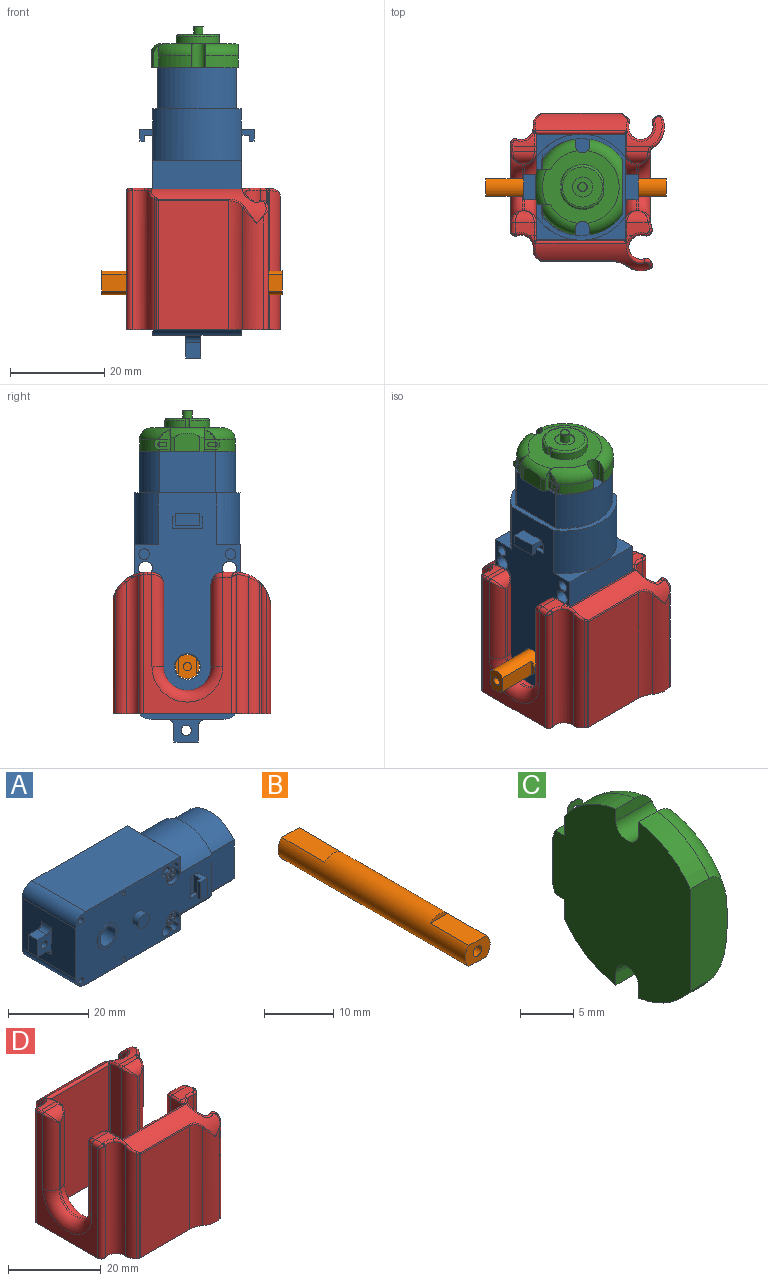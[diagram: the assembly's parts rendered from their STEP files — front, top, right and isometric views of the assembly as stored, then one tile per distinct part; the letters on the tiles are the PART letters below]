
ASSEMBLY  parts=4 mates=3
PART A: 126 faces, bbox 61.5x24.2x22.5 mm
  f0: torus R=1.4mm, axis (0,-1,0), area 4.7mm2, adj f2,f68
  f1: torus R=1.4mm, axis (0,-1,0), area 4.7mm2, adj f3,f66
  f2: cylinder r=1.7mm len=3.4mm, axis (0,1,0), area 12.8mm2, adj f0,f23,f67
  f3: cylinder r=1.7mm len=3.4mm, axis (0,1,0), area 12.8mm2, adj f1,f24,f65
  f4: cylinder r=2.25mm len=4.5mm, axis (0,-1,0), area 19.8mm2, adj f8,f9,f23,f26
  f5: cylinder r=2.25mm len=4.5mm, axis (0,-1,0), area 19.8mm2, adj f12,f13,f24,f26
  f6: cylinder r=1.12mm len=7.5mm, axis (0,1,0), area 53mm2, adj f37,f62
  f7: cylinder r=1.12mm len=7.5mm, axis (0,1,0), area 53mm2, adj f37,f61
  f8: cylinder r=1.5mm len=18.8mm, axis (0,-1,0), area 173.3mm2, adj f4,f23,f26,f37,f64
  f9: cylinder r=1.12mm len=7.5mm, axis (0,-1,0), area 48.7mm2, adj f4,f23,f26,f55,f64,f67
  f10: cylinder r=0.62mm len=7.5mm, axis (0,-1,0), area 29.5mm2, adj f26,f54
  f11: cylinder r=0.9mm len=7.5mm, axis (0,-1,0), area 42.4mm2, adj f26,f53
  f12: cylinder r=1.12mm len=7.5mm, axis (0,-1,0), area 48.7mm2, adj f5,f24,f26,f52,f63,f65
  f13: cylinder r=1.5mm len=18.8mm, axis (0,-1,0), area 173.3mm2, adj f5,f24,f26,f37,f63
  f14: cylinder r=0.62mm len=7.5mm, axis (0,-1,0), area 29.5mm2, adj f26,f51
  f15: cylinder r=0.9mm len=7.5mm, axis (0,-1,0), area 42.4mm2, adj f26,f50
  f16: cylinder r=2mm len=4mm, axis (0,1,0), area 25.1mm2, adj f26,f49
  f17: cylinder r=3.62mm len=7.25mm, axis (0,1,0), area 5.7mm2, adj f26,f48
  f18: cylinder r=2.75mm len=19.05mm, axis (0,1,0), area 329.2mm2, adj f37,f48
  f19: cylinder r=1.1mm len=3.2mm, axis (0,1,0), area 22.1mm2, adj f38,f40
  f20: plane 5.25x2.7mm, normal (-1,0,0), area 14.2mm2, adj f107,f113,f115,f125
  f21: plane 1x0.63mm, normal (-1,0,0), area 0.6mm2, adj f37,f109,f112,f118
  f22: plane 1x0.63mm, normal (-1,0,0), area 0.6mm2, adj f26,f103,f107,f113
  f23: plane 4.5x4.48mm, normal (0,-1,0), area 5.4mm2, adj f2,f4,f8,f9,f64
  f24: plane 4.5x4.48mm, normal (0,-1,0), area 5.4mm2, adj f3,f5,f12,f13,f63
  f25: plane 22.5x18.8mm, normal (1,0,0), area 66.1mm2, adj f26,f27,f37,f47,f56,f57,f58,f59
  f26: plane 48x22.3mm, normal (0,-1,0), area 823.8mm2, adj f4,f5,f8,f9,f10,f11,f12,f13
  f27: cylinder r=11.25mm len=18.8mm, axis (-1,0,0), area 244.8mm2, adj f25,f26,f28,f29,f37,f45
  f28: plane 7.9x4.97mm, normal (1,0,0), area 13.3mm2, adj f27,f33,f37
  f29: plane 7.9x4.97mm, normal (1,0,0), area 13.3mm2, adj f26,f27,f33
  f30: plane 7.9x4.97mm, normal (1,0,0), area 13.3mm2, adj f26,f36,f47
  f31: plane 7.9x4.97mm, normal (1,0,0), area 13.3mm2, adj f36,f37,f47
  f32: plane 18.8x15.3mm, normal (-1,0,0), area 261.4mm2, adj f26,f34,f35,f37,f38,f40,f43,f44
  f33: plane 33.5x18.8mm, normal (0,0,1), area 629.8mm2, adj f26,f28,f29,f34,f37,f45
  f34: cylinder r=3.5mm len=18.8mm, axis (0,1,0), area 103.4mm2, adj f26,f32,f33,f37
  f35: cylinder r=3.5mm len=18.8mm, axis (0,1,0), area 103.4mm2, adj f26,f32,f36,f37
  f36: plane 33.5x18.8mm, normal (0,0,-1), area 629.8mm2, adj f26,f30,f31,f35,f37,f46
  f37: plane 48x22.3mm, normal (0,1,0), area 890.3mm2, adj f6,f7,f8,f13,f18,f21,f25,f27
  f38: plane 8.2x4.8mm, normal (0,-1,0), area 22.1mm2, adj f19,f32,f39,f41,f42,f43,f44
  f39: plane 3.3x3.2mm, normal (0,0,1), area 10.6mm2, adj f38,f40,f42,f44
  f40: plane 8.2x4.8mm, normal (0,1,0), area 22.1mm2, adj f19,f32,f39,f41,f42,f43,f44
  f41: plane 3.3x3.2mm, normal (0,0,-1), area 10.6mm2, adj f38,f40,f42,f43
  f42: plane 5.2x3.2mm, normal (-1,0,0), area 16.6mm2, adj f38,f39,f40,f41
  f43: cylinder r=1.5mm len=3.2mm, axis (0,1,0), area 7.5mm2, adj f32,f38,f40,f41
  f44: cylinder r=1.5mm len=3.2mm, axis (0,-1,0), area 7.5mm2, adj f32,f38,f39,f40
  f45: plane 2.99x0.1mm, normal (-1,0,0), area 0.2mm2, adj f27,f33
  f46: plane 2.99x0.1mm, normal (-1,0,0), area 0.2mm2, adj f36,f47
  f47: cylinder r=11.25mm len=18.8mm, axis (-1,0,0), area 244.8mm2, adj f25,f26,f30,f31,f37,f46
  f48: plane 7.25x7.25mm, normal (0,-1,0), area 17.5mm2, adj f17,f18
  f49: plane 4x4mm, normal (0,-1,0), area 12.6mm2, adj f16
  f50: plane 1.8x1.8mm, normal (0,-1,0), area 2.5mm2, adj f15
  f51: plane 1.25x1.25mm, normal (0,-1,0), area 1.2mm2, adj f14
  f52: plane 2.25x2.25mm, normal (0,-1,0), area 4mm2, adj f12
  f53: plane 1.8x1.8mm, normal (0,-1,0), area 2.5mm2, adj f11
  f54: plane 1.25x1.25mm, normal (0,-1,0), area 1.2mm2, adj f10
  f55: plane 2.25x2.25mm, normal (0,-1,0), area 4mm2, adj f9
  f56: cylinder r=10.25mm len=16.8mm, axis (-1,0,0), area 172.1mm2, adj f25,f57,f59,f60
  f57: plane 11.75x8.74mm, normal (0,1,0), area 102.7mm2, adj f25,f56,f58,f60
  f58: cylinder r=10.25mm len=16.8mm, axis (-1,0,0), area 172.1mm2, adj f25,f57,f59,f60
  f59: plane 11.75x8.74mm, normal (0,-1,0), area 102.7mm2, adj f25,f56,f58,f60
  f60: plane 20.5x16.8mm, normal (1,0,0), area 300.5mm2, adj f56,f57,f58,f59
  f61: plane 2.25x2.25mm, normal (0,1,0), area 4mm2, adj f7
  f62: plane 2.25x2.25mm, normal (0,1,0), area 4mm2, adj f6
  f63: cylinder r=2.25mm len=2mm, axis (0,-1,0), area 0.9mm2, adj f12,f13,f24,f26
  f64: cylinder r=2.25mm len=2mm, axis (0,-1,0), area 0.9mm2, adj f8,f9,f23,f26
  f65: plane 0.76x0.22mm, normal (0,1,0), area 0.1mm2, adj f3,f12
  f66: plane 2.8x2.8mm, normal (0,-1,0), area 3.6mm2, adj f1,f69,f70,f71,f72,f73,f74,f75
  f67: plane 0.76x0.22mm, normal (0,1,0), area 0.1mm2, adj f2,f9
  f68: plane 2.8x2.8mm, normal (0,-1,0), area 3.6mm2, adj f0,f82,f83,f84,f85,f86,f87,f88
  f69: plane 1.5x0.84mm, normal (0.99,-0.16,0), area 0.9mm2, adj f66,f70,f81,f100
  f70: plane 1.5x0.6mm, normal (0,-0.16,-0.99), area 0.6mm2, adj f66,f69,f71,f81
  f71: plane 1.5x0.84mm, normal (-0.99,-0.16,0), area 0.9mm2, adj f66,f70,f81,f99
  f72: plane 1.5x0.84mm, normal (0,-0.16,-0.99), area 0.9mm2, adj f66,f73,f81,f99
  f73: plane 1.5x0.6mm, normal (-0.99,-0.16,0), area 0.6mm2, adj f66,f72,f74,f81
  f74: plane 1.5x0.84mm, normal (0,-0.16,0.99), area 0.9mm2, adj f66,f73,f81,f102
  f75: plane 1.5x0.84mm, normal (-0.99,-0.16,0), area 0.9mm2, adj f66,f76,f81,f102
  f76: plane 1.5x0.6mm, normal (0,-0.16,0.99), area 0.6mm2, adj f66,f75,f77,f81
  f77: plane 1.5x0.84mm, normal (0.99,-0.16,0), area 0.9mm2, adj f66,f76,f81,f101
  f78: plane 1.5x0.84mm, normal (0,-0.16,0.99), area 0.9mm2, adj f66,f79,f81,f101
  f79: plane 1.5x0.6mm, normal (0.99,-0.16,0), area 0.6mm2, adj f66,f78,f80,f81
  f80: plane 1.5x0.84mm, normal (0,-0.16,-0.99), area 0.9mm2, adj f66,f79,f81,f100
  f81: plane 1.93x1.93mm, normal (0,-1,0), area 0.5mm2, adj f69,f70,f71,f72,f73,f74,f75,f76
  f82: plane 1.5x0.84mm, normal (0,-0.16,0.99), area 0.9mm2, adj f68,f83,f94,f98
  f83: plane 1.5x0.6mm, normal (0.99,-0.16,0), area 0.6mm2, adj f68,f82,f84,f94
  f84: plane 1.5x0.84mm, normal (0,-0.16,-0.99), area 0.9mm2, adj f68,f83,f94,f96
  f85: plane 1.5x0.84mm, normal (0.99,-0.16,0), area 0.9mm2, adj f68,f86,f94,f96
  f86: plane 1.5x0.6mm, normal (0,-0.16,-0.99), area 0.6mm2, adj f68,f85,f87,f94
  f87: plane 1.5x0.84mm, normal (-0.99,-0.16,0), area 0.9mm2, adj f68,f86,f94,f95
  f88: plane 1.5x0.84mm, normal (0,-0.16,-0.99), area 0.9mm2, adj f68,f89,f94,f95
  f89: plane 1.5x0.6mm, normal (-0.99,-0.16,0), area 0.6mm2, adj f68,f88,f90,f94
  f90: plane 1.5x0.84mm, normal (0,-0.16,0.99), area 0.9mm2, adj f68,f89,f94,f97
  f91: plane 1.5x0.84mm, normal (-0.99,-0.16,0), area 0.9mm2, adj f68,f92,f94,f97
  f92: plane 1.5x0.6mm, normal (0,-0.16,0.99), area 0.6mm2, adj f68,f91,f93,f94
  f93: plane 1.5x0.84mm, normal (0.99,-0.16,0), area 0.9mm2, adj f68,f92,f94,f98
  f94: plane 1.93x1.93mm, normal (0,-1,0), area 0.5mm2, adj f82,f83,f84,f85,f86,f87,f88,f89
  f95: cylinder r=0.3mm len=1.54mm, axis (0.15,-0.98,0.15), area 0.7mm2, adj f68,f87,f88,f94
  f96: cylinder r=0.3mm len=1.54mm, axis (-0.15,-0.98,0.15), area 0.7mm2, adj f68,f84,f85,f94
  f97: cylinder r=0.3mm len=1.54mm, axis (0.15,-0.98,-0.15), area 0.7mm2, adj f68,f90,f91,f94
  f98: cylinder r=0.3mm len=1.54mm, axis (-0.15,-0.98,-0.15), area 0.7mm2, adj f68,f82,f93,f94
  f99: cylinder r=0.3mm len=1.54mm, axis (0.15,-0.98,0.15), area 0.7mm2, adj f66,f71,f72,f81
  f100: cylinder r=0.3mm len=1.54mm, axis (-0.15,-0.98,0.15), area 0.7mm2, adj f66,f69,f80,f81
  f101: cylinder r=0.3mm len=1.54mm, axis (-0.15,-0.98,-0.15), area 0.7mm2, adj f66,f77,f78,f81
  f102: cylinder r=0.3mm len=1.54mm, axis (0.15,-0.98,-0.15), area 0.7mm2, adj f66,f74,f75,f81
  f103: plane 2.5x1mm, normal (0,0,-1), area 2.5mm2, adj f22,f26,f106,f107
  f104: plane 1x0.63mm, normal (-1,0,0), area 0.6mm2, adj f26,f105,f107,f115
  f105: plane 2.5x1mm, normal (0,0,1), area 2.5mm2, adj f26,f104,f106,f107
  f106: plane 6.5x1mm, normal (1,0,0), area 6.5mm2, adj f26,f103,f105,f107
  f107: plane 6.5x2.5mm, normal (0,-1,0), area 12.8mm2, adj f20,f22,f103,f104,f105,f106,f113,f115
  f108: plane 1x0.63mm, normal (-1,0,0), area 0.6mm2, adj f37,f111,f112,f119
  f109: plane 2.5x1mm, normal (0,0,-1), area 2.5mm2, adj f21,f37,f110,f112
  f110: plane 6.5x1mm, normal (1,0,0), area 6.5mm2, adj f37,f109,f111,f112
  f111: plane 2.5x1mm, normal (0,0,1), area 2.5mm2, adj f37,f108,f110,f112
  f112: plane 6.5x2.5mm, normal (0,1,0), area 12.8mm2, adj f21,f108,f109,f110,f111,f118,f119,f120
  f113: plane 3.7x2.5mm, normal (0,0,1), area 5.4mm2, adj f20,f22,f26,f107,f114,f116,f124,f125
  f114: plane 5.25x2.7mm, normal (1,0,0), area 14.2mm2, adj f26,f113,f115,f116
  f115: plane 3.7x2.5mm, normal (0,0,-1), area 5.4mm2, adj f20,f26,f104,f107,f114,f116,f124,f125
  f116: plane 5.25x2.5mm, normal (0,-1,0), area 13.1mm2, adj f113,f114,f115,f124
  f117: plane 5.25x2.7mm, normal (1,0,0), area 14.2mm2, adj f37,f118,f119,f121
  f118: plane 3.7x2.5mm, normal (0,0,1), area 5.4mm2, adj f21,f37,f112,f117,f120,f121,f122,f123
  f119: plane 3.7x2.5mm, normal (0,0,-1), area 5.4mm2, adj f37,f108,f112,f117,f120,f121,f122,f123
  f120: plane 5.25x2.7mm, normal (-1,0,0), area 14.2mm2, adj f112,f118,f119,f123
  f121: plane 5.25x2.5mm, normal (0,1,0), area 13.1mm2, adj f117,f118,f119,f122
  f122: plane 5.25x1mm, normal (-1,0,0), area 5.3mm2, adj f118,f119,f121,f123
  f123: plane 5.25x1.2mm, normal (0,-1,0), area 6.3mm2, adj f118,f119,f120,f122
  f124: plane 5.25x1mm, normal (-1,0,0), area 5.2mm2, adj f113,f115,f116,f125
  f125: plane 5.25x1.2mm, normal (0,1,0), area 6.3mm2, adj f20,f113,f115,f124
PART B: 15 faces, bbox 5.1x38.2x5.1 mm
  f0: cylinder r=0.88mm len=8.75mm, axis (0,1,0), area 48.1mm2, adj f4,f14
  f1: cylinder r=0.88mm len=7.85mm, axis (0,-1,0), area 43.2mm2, adj f3,f5
  f2: cylinder r=2.55mm len=38.2mm, axis (0,1,0), area 483.5mm2, adj f3,f4,f6,f7,f8,f9,f10,f11
  f3: plane 5.1x3.7mm, normal (0,-1,0), area 14.6mm2, adj f1,f2,f6,f8
  f4: plane 5.1x3.7mm, normal (0,1,0), area 14.6mm2, adj f0,f2,f10,f12
  f5: plane 1.75x1.75mm, normal (0,-1,0), area 2.4mm2, adj f1
  f6: plane 7.85x3.51mm, normal (0,0,1), area 27.6mm2, adj f2,f3,f7
  f7: plane 3.51x0.7mm, normal (0,-1,0), area 1.7mm2, adj f2,f6
  f8: plane 7.85x3.51mm, normal (0,0,-1), area 27.6mm2, adj f2,f3,f9
  f9: plane 3.51x0.7mm, normal (0,-1,0), area 1.7mm2, adj f2,f8
  f10: plane 8.75x3.51mm, normal (0,0,1), area 30.7mm2, adj f2,f4,f11
  f11: plane 3.51x0.7mm, normal (0,1,0), area 1.7mm2, adj f2,f10
  f12: plane 8.75x3.51mm, normal (0,0,-1), area 30.7mm2, adj f2,f4,f13
  f13: plane 3.51x0.7mm, normal (0,1,0), area 1.7mm2, adj f2,f12
  f14: plane 1.75x1.75mm, normal (0,1,0), area 2.4mm2, adj f0
PART C: 61 faces, bbox 9.7x22.2x22.9 mm
  f0: cylinder r=0.43mm len=0.86mm, axis (0,-1,0), area 0.1mm2, adj f51,f52,f58,f60
  f1: cylinder r=0.43mm len=0.86mm, axis (0,-1,0), area 0.1mm2, adj f22,f40,f47,f48
  f2: torus R=0.9mm, axis (1,0,0), area 1mm2, adj f3,f37
  f3: cylinder r=1mm len=2mm, axis (-1,0,0), area 11.9mm2, adj f2,f16
  f4: cylinder r=2.12mm len=4.25mm, axis (1,0,0), area 2.7mm2, adj f16,f36
  f5: torus R=4.25mm, axis (1,0,0), area 20.7mm2, adj f6,f33,f34,f35,f36
  f6: cylinder r=0.5mm len=2mm, axis (-1,0,0), area 2.7mm2, adj f5,f13,f33,f34
  f7: plane 3.09x2.95mm, normal (0,1,0), area 3.3mm2, adj f9,f32,f53
  f8: plane 2.2x0.5mm, normal (0,1,0), area 1.1mm2, adj f9,f21,f29,f57
  f9: plane 5.29x3.04mm, normal (0,0,-1), area 4.7mm2, adj f7,f8,f13,f29,f32,f38,f50,f52
  f10: plane 1.54x0.86mm, normal (0,1,0), area 1.2mm2, adj f21,f58,f59,f60
  f11: plane 2.2x0.5mm, normal (0,1,0), area 1.1mm2, adj f15,f23,f29,f41
  f12: plane 3.09x2.95mm, normal (0,1,0), area 3.3mm2, adj f15,f30,f45
  f13: plane 16.23x15.36mm, normal (1,0,0), area 123.2mm2, adj f6,f9,f15,f19,f25,f30,f31,f32
  f14: plane 5.31x3.87mm, normal (0,1,0), area 19.3mm2, adj f29,f38,f49,f50
  f15: plane 5.29x3.04mm, normal (0,0,1), area 4.7mm2, adj f11,f12,f13,f29,f30,f38,f40,f41
  f16: plane 4.25x4.25mm, normal (1,0,0), area 11mm2, adj f3,f4
  f17: cylinder r=10.25mm len=6.9mm, axis (-1,0,0), area 20.9mm2, adj f18,f28,f29,f31
  f18: plane 4.85x1.51mm, normal (0,1,0), area 5.7mm2, adj f17,f19,f29,f31
  f19: cylinder r=1.5mm len=5mm, axis (-1,0,0), area 23.2mm2, adj f13,f18,f20,f29,f31,f32
  f20: plane 4.85x1.51mm, normal (0,-1,0), area 5.7mm2, adj f19,f21,f29,f32
  f21: cylinder r=10.25mm len=6.9mm, axis (-1,0,0), area 20.9mm2, adj f8,f10,f20,f29,f32,f51
  f22: plane 1.54x0.86mm, normal (0,1,0), area 1.2mm2, adj f1,f23,f47,f48
  f23: cylinder r=10.25mm len=6.9mm, axis (-1,0,0), area 20.9mm2, adj f11,f22,f24,f29,f30,f39
  f24: plane 4.85x1.51mm, normal (0,-1,0), area 5.7mm2, adj f23,f25,f29,f30
  f25: cylinder r=1.5mm len=5mm, axis (-1,0,0), area 23.2mm2, adj f13,f24,f26,f29,f30,f31
  f26: plane 4.85x1.51mm, normal (0,1,0), area 5.7mm2, adj f25,f27,f29,f31
  f27: cylinder r=10.25mm len=6.9mm, axis (-1,0,0), area 20.9mm2, adj f26,f28,f29,f31
  f28: plane 11.75x4.92mm, normal (0,-1,0), area 52.9mm2, adj f17,f27,f29,f31
  f29: plane 20.28x18.3mm, normal (-1,0,0), area 295.4mm2, adj f8,f9,f11,f14,f15,f17,f18,f19
  f30: torus R=7.75mm, axis (1,0,0), area 33.7mm2, adj f12,f13,f15,f23,f24,f25
  f31: torus R=7.75mm, axis (1,0,0), area 72.9mm2, adj f13,f17,f18,f19,f25,f26,f27,f28
  f32: torus R=7.75mm, axis (1,0,0), area 33.7mm2, adj f7,f9,f13,f19,f20,f21
  f33: cylinder r=4.75mm len=9.12mm, axis (-1,0,0), area 18.9mm2, adj f5,f6,f13,f35
  f34: cylinder r=4.75mm len=9.12mm, axis (-1,0,0), area 18.9mm2, adj f5,f6,f13,f35
  f35: plane 4.08x2.48mm, normal (0,-1,0), area 6.8mm2, adj f5,f13,f33,f34
  f36: plane 8.5x8.5mm, normal (1,0,0), area 42.6mm2, adj f4,f5
  f37: plane 1.8x1.8mm, normal (1,0,0), area 2.5mm2, adj f2
  f38: revolved ~8.87x2.61mm, area 18mm2, adj f9,f13,f14,f15,f49,f50
  f39: plane 2x1.03mm, normal (0,-1,0), area 1.5mm2, adj f23,f41,f42,f43,f44,f45,f46,f47
  f40: plane 3.23x2mm, normal (0,1,0), area 4.7mm2, adj f1,f15,f41,f42,f43,f44,f45,f46
  f41: plane 2.73x0.1mm, normal (-1,0,0), area 0.3mm2, adj f11,f15,f39,f40,f42
  f42: plane 0.5x0.5mm, normal (-0.71,0,0.71), area 0.1mm2, adj f39,f40,f41,f43
  f43: plane 1x0.1mm, normal (0,0,1), area 0.1mm2, adj f39,f40,f42,f44
  f44: plane 0.5x0.5mm, normal (0.71,0,0.71), area 0.1mm2, adj f39,f40,f43,f45
  f45: plane 2.73x0.1mm, normal (1,0,0), area 0.3mm2, adj f12,f15,f39,f40,f44
  f46: cylinder r=0.43mm len=0.86mm, axis (0,-1,0), area 0.1mm2, adj f39,f40,f47,f48
  f47: plane 1.14x0.1mm, normal (-1,0,0), area 0.1mm2, adj f1,f22,f39,f40,f46
  f48: plane 1.14x0.1mm, normal (1,0,0), area 0.1mm2, adj f1,f22,f39,f40,f46
  f49: cylinder r=10.25mm len=3mm, axis (1,0,0), area 3.2mm2, adj f14,f15,f29,f38
  f50: cylinder r=10.25mm len=3mm, axis (1,0,0), area 3.2mm2, adj f9,f14,f29,f38
  f51: plane 2x1.03mm, normal (0,-1,0), area 1.5mm2, adj f0,f21,f53,f54,f55,f56,f57,f58
  f52: plane 3.23x2mm, normal (0,1,0), area 4.7mm2, adj f0,f9,f53,f54,f55,f56,f57,f58
  f53: plane 2.73x0.1mm, normal (1,0,0), area 0.3mm2, adj f7,f9,f51,f52,f54
  f54: plane 0.5x0.5mm, normal (0.71,0,-0.71), area 0.1mm2, adj f51,f52,f53,f55
  f55: plane 1x0.1mm, normal (0,0,-1), area 0.1mm2, adj f51,f52,f54,f56
  f56: plane 0.5x0.5mm, normal (-0.71,0,-0.71), area 0.1mm2, adj f51,f52,f55,f57
  f57: plane 2.73x0.1mm, normal (-1,0,0), area 0.3mm2, adj f8,f9,f51,f52,f56
  f58: plane 1.14x0.1mm, normal (1,0,0), area 0.1mm2, adj f0,f10,f51,f52,f59
  f59: cylinder r=0.43mm len=0.86mm, axis (0,-1,0), area 0.1mm2, adj f10,f52,f58,f60
  f60: plane 1.14x0.1mm, normal (-1,0,0), area 0.1mm2, adj f0,f10,f51,f52,f59
PART D: 176 faces, bbox 32.6x33.5x33 mm
  f0: plane 33.4x32.6mm, normal (0,0,-1), area 424.7mm2, adj f3,f4,f7,f8,f9,f10,f11,f13
  f1: cylinder r=7.5mm len=4.5mm, axis (-1,0,0), area 7.1mm2, adj f6,f92,f137,f138,f139
  f2: cylinder r=7.5mm len=1.32mm, axis (-1,0,0), area 0.7mm2, adj f25,f85,f87
  f3: plane 29.5x22.12mm, normal (1,0,0), area 269.2mm2, adj f0,f34,f35,f37,f82,f85,f91,f92
  f4: plane 29.5x22.12mm, normal (-1,0,0), area 269.2mm2, adj f0,f46,f48,f49,f81,f83,f95,f96
  f5: plane 4.91x1.03mm, normal (0,0,1), area 4.8mm2, adj f32,f44,f70,f95
  f6: plane 4.5x1.03mm, normal (0,0,1), area 4.6mm2, adj f1,f36,f91,f140
  f7: cylinder r=2.58mm len=29.41mm, axis (0,0,-1), area 150.8mm2, adj f0,f51,f114,f133,f135,f137
  f8: cylinder r=2.58mm len=29.5mm, axis (0,0,-1), area 152.3mm2, adj f0,f52,f84,f87,f110
  f9: plane 27.73x0.56mm, normal (-0.58,-0.82,0), area 18.9mm2, adj f0,f52,f89,f146
  f10: plane 27.35x15.02mm, normal (0,-1,0), area 410.7mm2, adj f0,f67,f144,f146
  f11: cylinder r=5mm len=25.89mm, axis (0,0,-1), area 111.4mm2, adj f0,f56,f67,f115,f142
  f12: plane 26.55x0.02mm, normal (0.82,0.58,0), area 0.7mm2, adj f54,f56,f117
  f13: cylinder r=2.58mm len=29.5mm, axis (0,0,-1), area 274mm2, adj f0,f54,f55,f119,f120
  f14: plane 29.5x0.1mm, normal (0.82,-0.58,0), area 3.8mm2, adj f0,f55,f60,f122
  f15: cylinder r=5mm len=29.49mm, axis (0,0,-1), area 190.4mm2, adj f0,f57,f61,f62,f63,f72
  f16: plane 26.33x0.02mm, normal (-0.58,0.82,0), area 0.7mm2, adj f57,f58,f74
  f17: cylinder r=2.58mm len=27.31mm, axis (0,0,-1), area 262.4mm2, adj f0,f58,f59,f76
  f18: plane 26.33x1.09mm, normal (0.58,0.82,0), area 34.1mm2, adj f0,f59,f78,f127
  f19: plane 29.33x18.2mm, normal (0,1,0), area 533.7mm2, adj f0,f86,f100,f103
  f20: plane 28.73x18.2mm, normal (0,-1,0), area 522.9mm2, adj f0,f94,f97,f106
  f21: plane 24.55x15.6mm, normal (0,1,0), area 383mm2, adj f0,f50,f53,f130
  f22: plane 4.92x2.68mm, normal (0,0,1), area 11.1mm2, adj f33,f47,f81,f120,f121,f122,f123,f124
  f23: plane 29.5x18.67mm, normal (-1,0,0), area 168.8mm2, adj f0,f38,f40,f41,f110,f112,f114,f139
  f24: plane 14.16x8.87mm, normal (1,0,0), area 55mm2, adj f0,f43,f61,f64
  f25: plane 4x2.68mm, normal (0,0,1), area 9.4mm2, adj f2,f39,f82,f84,f109,f112
  f26: cylinder r=5mm len=10mm, axis (1,0,0), area 7.9mm2, adj f27,f28,f43,f48
  f27: plane 17.5x0.5mm, normal (0,1,0), area 8.8mm2, adj f26,f45,f47,f49
  f28: plane 17.5x0.5mm, normal (0,-1,0), area 8.8mm2, adj f26,f42,f44,f46
  f29: cylinder r=5mm len=10mm, axis (1,0,0), area 7.9mm2, adj f30,f31,f35,f40
  f30: plane 17.5x0.5mm, normal (0,-1,0), area 8.8mm2, adj f29,f34,f36,f38
  f31: plane 17.5x0.5mm, normal (0,1,0), area 8.8mm2, adj f29,f37,f39,f41
  f32: cylinder r=7.5mm len=26.99mm, axis (-1,0,0), area 131mm2, adj f5,f71,f72,f73,f74,f75,f76,f77
  f33: cylinder r=7.5mm len=24.43mm, axis (-1,0,0), area 103.5mm2, adj f22,f83,f86,f87,f88,f89,f115,f116
  f34: cylinder r=2.5mm len=19.5mm, axis (0,0,-1), area 72.6mm2, adj f3,f30,f35,f90
  f35: torus R=7.5mm, axis (1,0,0), area 72.9mm2, adj f3,f29,f34,f37
  f36: cylinder r=2.5mm len=4.5mm, axis (1,0,0), area 12mm2, adj f6,f30,f90,f141
  f37: cylinder r=2.5mm len=19.5mm, axis (0,0,1), area 72.6mm2, adj f3,f31,f35,f80
  f38: cylinder r=2.5mm len=19.5mm, axis (0,0,1), area 72.6mm2, adj f23,f30,f40,f141
  f39: cylinder r=2.5mm len=4mm, axis (-1,0,0), area 10.7mm2, adj f25,f31,f80,f113
  f40: torus R=7.5mm, axis (1,0,0), area 72.9mm2, adj f23,f29,f38,f41
  f41: cylinder r=2.5mm len=19mm, axis (0,0,-1), area 71.7mm2, adj f23,f31,f40,f113
  f42: cylinder r=2.5mm len=19.5mm, axis (0,0,-1), area 71.6mm2, adj f28,f43,f63,f68
  f43: torus R=7.5mm, axis (1,0,0), area 72.4mm2, adj f24,f26,f42,f45,f62,f65
  f44: cylinder r=2.5mm len=4.5mm, axis (1,0,0), area 12mm2, adj f5,f28,f68,f69,f93
  f45: cylinder r=2.5mm len=19.49mm, axis (0,0,1), area 67.2mm2, adj f27,f43,f66,f126
  f46: cylinder r=2.5mm len=19.5mm, axis (0,0,1), area 72.6mm2, adj f4,f28,f48,f93
  f47: cylinder r=2.5mm len=4.52mm, axis (-1,0,0), area 12mm2, adj f22,f27,f79,f125,f126
  f48: torus R=7.5mm, axis (1,0,0), area 72.9mm2, adj f4,f26,f46,f49
  f49: cylinder r=2.5mm len=19.5mm, axis (0,0,-1), area 72.6mm2, adj f4,f27,f48,f79
  f50: cylinder r=2.5mm len=25.48mm, axis (0,0,-1), area 38mm2, adj f0,f21,f51,f131,f132
  f51: cylinder r=2.5mm len=27.85mm, axis (0,0,-1), area 69.9mm2, adj f0,f7,f50,f132
  f52: cylinder r=2.5mm len=28.91mm, axis (0,0,-1), area 74.7mm2, adj f0,f8,f9,f88
  f53: cylinder r=2.5mm len=24.74mm, axis (0,0,-1), area 15.3mm2, adj f0,f21,f127,f129
  f54: bspline ~31.27x1.33mm, area 40.5mm2, adj f0,f12,f13,f118
  f55: bspline ~33x1.33mm, area 44.7mm2, adj f0,f13,f14,f121
  f56: bspline ~30.43x1.84mm, area 62.3mm2, adj f0,f11,f12,f116
  f57: bspline ~30.17x1.84mm, area 65.3mm2, adj f0,f15,f16,f73
  f58: bspline ~30.96x1.33mm, area 40.6mm2, adj f0,f16,f17,f75
  f59: bspline ~30.96x1.33mm, area 40.6mm2, adj f0,f17,f18,f77
  f60: bspline ~33x1.56mm, area 34.1mm2, adj f0,f14,f64,f65,f66,f123
  f61: bspline ~33x1.03mm, area 11mm2, adj f0,f15,f24,f62
  f62: bspline ~1.13x1.03mm, area 1.4mm2, adj f15,f43,f61,f63
  f63: bspline ~21x1mm, area 23.6mm2, adj f15,f42,f62,f69,f70,f71
  f64: cylinder r=5mm len=6.73mm, axis (0,0,-1), area 12.6mm2, adj f0,f24,f60,f65
  f65: bspline ~6.31x2.67mm, area 5.1mm2, adj f43,f60,f64,f66
  f66: cylinder r=5mm len=19.5mm, axis (0,0,-1), area 27.4mm2, adj f45,f60,f65,f124,f125
  f67: cylinder r=5mm len=27.35mm, axis (0,0,-1), area 84.5mm2, adj f0,f10,f11,f143
  f68: bspline ~2.6x2.5mm, area 1.3mm2, adj f42,f44,f69
  f69: bspline ~0.51x0.51mm, area 0mm2, adj f44,f63,f68,f70
  f70: bspline ~1.3x0.84mm, area 0.7mm2, adj f5,f63,f69,f71
  f71: bspline ~1.03x0.92mm, area 0.4mm2, adj f32,f63,f70,f72
  f72: bspline ~7.05x4.45mm, area 6mm2, adj f15,f32,f71,f73
  f73: bspline ~1.88x1.36mm, area 1.2mm2, adj f32,f57,f72,f74
  f74: bspline ~0.31x0.3mm, area 0mm2, adj f16,f32,f73,f75
  f75: bspline ~1.57x1.53mm, area 1.1mm2, adj f32,f58,f74,f76
  f76: bspline ~6.16x5.13mm, area 8.7mm2, adj f17,f32,f75,f77
  f77: bspline ~1.52x1.5mm, area 1.1mm2, adj f32,f59,f76,f78
  f78: bspline ~1.86x1.38mm, area 0.8mm2, adj f18,f32,f77,f128
  f79: bspline ~2.89x2.5mm, area 1.3mm2, adj f47,f49,f81
  f80: bspline ~2.89x2.5mm, area 1.3mm2, adj f37,f39,f82
  f81: cylinder r=0.5mm len=2.68mm, axis (0,1,0), area 2.1mm2, adj f4,f22,f79,f83
  f82: cylinder r=0.5mm len=2.68mm, axis (0,-1,0), area 2.1mm2, adj f3,f25,f80,f85
  f83: torus R=7mm, axis (1,0,0), area 1mm2, adj f4,f33,f81,f105
  f84: torus R=3.08mm, axis (0,0,1), area 2.1mm2, adj f8,f25,f87,f109
  f85: torus R=7mm, axis (1,0,0), area 1mm2, adj f2,f3,f82,f87,f102
  f86: cylinder r=0.5mm len=19.54mm, axis (-1,0,0), area 16.7mm2, adj f19,f33,f87,f101,f102,f104,f105
  f87: bspline ~3.91x1.7mm, area 2.4mm2, adj f2,f8,f33,f84,f85,f86,f88,f102
  f88: bspline ~2.95x1.92mm, area 1.8mm2, adj f33,f52,f87,f89
  f89: bspline ~0.85x0.76mm, area 0.4mm2, adj f9,f33,f88,f145
  f90: bspline ~2.6x2.5mm, area 1.3mm2, adj f34,f36,f91
  f91: cylinder r=0.5mm len=1.03mm, axis (0,-1,0), area 0.8mm2, adj f3,f6,f90,f92
  f92: torus R=7mm, axis (1,0,0), area 2.4mm2, adj f1,f3,f91,f99,f136
  f93: bspline ~2.6x2.5mm, area 1.3mm2, adj f44,f46,f95
  f94: cylinder r=0.5mm len=19.49mm, axis (-1,0,0), area 19mm2, adj f20,f32,f98,f99,f107,f108,f134
  f95: cylinder r=0.5mm len=1.03mm, axis (0,1,0), area 0.8mm2, adj f4,f5,f93,f96
  f96: torus R=7mm, axis (1,0,0), area 2.4mm2, adj f4,f32,f95,f108
  f97: cylinder r=0.2mm len=28.73mm, axis (0,0,-1), area 9mm2, adj f0,f3,f20,f98
  f98: torus R=0.7mm, axis (1,0,0), area 0.1mm2, adj f3,f94,f97,f99
  f99: bspline ~0.89x0.7mm, area 0.2mm2, adj f92,f94,f98,f135
  f100: cylinder r=0.2mm len=29.33mm, axis (0,0,1), area 9.2mm2, adj f0,f3,f19,f101
  f101: torus R=0.7mm, axis (1,0,0), area 0mm2, adj f3,f86,f100,f102
  f102: bspline ~0.81x0.7mm, area 0.2mm2, adj f85,f86,f87,f101
  f103: cylinder r=0.2mm len=29.33mm, axis (0,0,-1), area 9.2mm2, adj f0,f4,f19,f104
  f104: torus R=0.7mm, axis (1,0,0), area 0mm2, adj f4,f86,f103,f105
  f105: bspline ~0.81x0.7mm, area 0.1mm2, adj f83,f86,f104
  f106: cylinder r=0.2mm len=28.73mm, axis (0,0,1), area 9mm2, adj f0,f4,f20,f107
  f107: torus R=0.7mm, axis (1,0,0), area 0.1mm2, adj f4,f94,f106,f108
  f108: bspline ~0.89x0.7mm, area 0.1mm2, adj f94,f96,f107
  f109: torus R=0.5mm, axis (0,0,1), area 0.2mm2, adj f25,f84,f110,f111
  f110: cylinder r=1mm len=29.5mm, axis (0,0,-1), area 56mm2, adj f0,f8,f23,f109,f111
  f111: bspline ~1.05x1mm, area 0.5mm2, adj f109,f110,f112
  f112: cylinder r=1mm len=2.31mm, axis (0,1,0), area 3.2mm2, adj f23,f25,f111,f113
  f113: bspline ~2.95x2.5mm, area 2.7mm2, adj f39,f41,f112
  f114: cylinder r=1mm len=29.45mm, axis (0,0,-1), area 56.3mm2, adj f0,f7,f23,f138
  f115: bspline ~2.7x2.22mm, area 0.1mm2, adj f11,f33,f116
  f116: bspline ~3.63x2.04mm, area 2.1mm2, adj f33,f56,f115,f117
  f117: bspline ~1.85x1.58mm, area 0mm2, adj f12,f33,f116,f118
  f118: bspline ~2.2x1.87mm, area 1.9mm2, adj f33,f54,f117,f119
  f119: bspline ~6.34x4.61mm, area 8.1mm2, adj f13,f33,f118,f120
  f120: torus R=3.08mm, axis (0,0,1), area 2mm2, adj f13,f22,f119,f121
  f121: bspline ~2x1.17mm, area 1mm2, adj f22,f55,f120,f122
  f122: cylinder r=0.5mm len=0.5mm, axis (-0.58,-0.82,0), area 0.1mm2, adj f14,f22,f121,f123
  f123: bspline ~1.57x0.99mm, area 0.8mm2, adj f22,f60,f122,f124
  f124: torus R=5.5mm, axis (0,0,1), area 1mm2, adj f22,f66,f123,f125
  f125: bspline ~1.49x0.68mm, area 0.2mm2, adj f47,f66,f124,f126
  f126: bspline ~2.5x2.5mm, area 1.2mm2, adj f45,f47,f125
  f127: cylinder r=0.5mm len=24.74mm, axis (0,0,-1), area 4.6mm2, adj f0,f18,f53,f128
  f128: sphere r=0.5mm, area 0mm2, adj f78,f127,f129
  f129: bspline ~0.98x0.59mm, area 0.1mm2, adj f32,f53,f128,f130
  f130: cylinder r=0.5mm len=15.6mm, axis (-1,0,0), area 2.3mm2, adj f21,f32,f129,f131
  f131: bspline ~1.76x1.51mm, area 0.4mm2, adj f32,f50,f130,f132
  f132: bspline ~3.16x2.75mm, area 2.1mm2, adj f32,f50,f51,f131,f133
  f133: bspline ~2.7x2.27mm, area 1.2mm2, adj f7,f32,f132,f134
  f134: sphere r=0.5mm, area 0mm2, adj f94,f133,f135
  f135: bspline ~0.76x0.75mm, area 0.2mm2, adj f7,f99,f134,f136
  f136: sphere r=0.5mm, area 0mm2, adj f92,f135,f137
  f137: bspline ~4.61x2.56mm, area 3mm2, adj f1,f7,f136,f138
  f138: bspline ~1.54x1.22mm, area 1.1mm2, adj f1,f114,f137,f139
  f139: torus R=7mm, axis (1,0,0), area 0.7mm2, adj f1,f23,f138,f140
  f140: cylinder r=0.5mm len=1.03mm, axis (0,1,0), area 0.8mm2, adj f6,f23,f139,f141
  f141: bspline ~2.6x2.5mm, area 1.3mm2, adj f36,f38,f140
  f142: bspline ~4.79x3.84mm, area 0.6mm2, adj f11,f33,f143
  f143: bspline ~4.61x2.66mm, area 1.5mm2, adj f33,f67,f142,f144
  f144: cylinder r=0.5mm len=15.02mm, axis (-1,0,0), area 5.7mm2, adj f10,f33,f143,f145
  f145: sphere r=0.5mm, area 0.1mm2, adj f89,f144,f146
  f146: cylinder r=0.5mm len=27.35mm, axis (0,0,-1), area 8.5mm2, adj f0,f9,f10,f145
  f147: plane 3.29x0.5mm, normal (1,0,0), area 1.6mm2, adj f0,f148,f154,f155
  f148: plane 0.85x0.5mm, normal (0,1,0), area 0.4mm2, adj f0,f147,f149,f155
  f149: plane 3.29x0.5mm, normal (-1,0,0), area 1.6mm2, adj f0,f148,f150,f155
  f150: plane 1.09x0.5mm, normal (0,1,0), area 0.5mm2, adj f0,f149,f151,f155
  f151: plane 0.71x0.5mm, normal (-1,0,0), area 0.4mm2, adj f0,f150,f152,f155
  f152: plane 3.02x0.5mm, normal (0,-1,0), area 1.5mm2, adj f0,f151,f153,f155
  f153: plane 0.71x0.5mm, normal (1,0,0), area 0.4mm2, adj f0,f152,f154,f155
  f154: plane 1.09x0.5mm, normal (0,1,0), area 0.5mm2, adj f0,f147,f153,f155
  f155: plane 4x3.02mm, normal (0,0,-1), area 4.9mm2, adj f147,f148,f149,f150,f151,f152,f153,f154
  f156: plane 0.78x0.5mm, normal (0,1,0), area 0.4mm2, adj f0,f157,f174,f175
  f157: plane 3.14x0.96mm, normal (-0.96,0.29,0), area 1.6mm2, adj f0,f156,f158,f175
  f158: plane 0.5x0.02mm, normal (0,1,0), area 0mm2, adj f0,f157,f159,f175
  f159: extruded ~1.28x0.5mm, area 0.6mm2, adj f0,f158,f160,f175
  f160: plane 1.86x0.5mm, normal (1,0,0), area 0.9mm2, adj f0,f159,f161,f175
  f161: plane 0.76x0.5mm, normal (0,1,0), area 0.4mm2, adj f0,f160,f162,f175
  f162: plane 4x0.5mm, normal (-1,0,0), area 2mm2, adj f0,f161,f163,f175
  f163: plane 1.15x0.5mm, normal (0,-1,0), area 0.6mm2, adj f0,f162,f164,f175
  f164: plane 3.06x0.95mm, normal (0.96,-0.3,0), area 1.6mm2, adj f0,f163,f165,f175
  f165: plane 0.5x0.02mm, normal (0,-1,0), area 0mm2, adj f0,f164,f166,f175
  f166: plane 3.06x1mm, normal (-0.95,-0.31,0), area 1.6mm2, adj f0,f165,f167,f175
  f167: plane 1.15x0.5mm, normal (0,-1,0), area 0.6mm2, adj f0,f166,f168,f175
  f168: plane 4x0.5mm, normal (1,0,0), area 2mm2, adj f0,f167,f169,f175
  f169: plane 0.79x0.5mm, normal (0,1,0), area 0.4mm2, adj f0,f168,f170,f175
  f170: plane 1.89x0.5mm, normal (-1,0,0), area 0.9mm2, adj f0,f169,f171,f175
  f171: extruded ~0.5x0.31mm, area 0.2mm2, adj f0,f170,f172,f175
  f172: extruded ~0.93x0.5mm, area 0.5mm2, adj f0,f171,f173,f175
  f173: plane 0.5x0.02mm, normal (0,1,0), area 0mm2, adj f0,f172,f174,f175
  f174: plane 3.13x1.03mm, normal (0.95,0.31,0), area 1.6mm2, adj f0,f156,f173,f175
  f175: plane 4.27x4mm, normal (0,0,-1), area 11mm2, adj f156,f157,f158,f159,f160,f161,f162,f163
PLACE A rot(axis=(0.58,-0.58,0.58),120deg) t=(151.6,29.51,48.2)mm
PLACE B rot(axis=(0.58,-0.58,0.58),120deg) t=(150.55,29.51,48.2)mm
PLACE C rot(axis=(0.58,-0.58,0.58),120deg) t=(151.93,29.51,48.2)mm
PLACE D t=(162.48,5.69,12.35)mm
MATE fastened B.f0 <-> A.f17  axis (-1,0,0) through (149.6,18.36,22.35)mm
MATE fastened A.f17 <-> D.f26  axis (-1,0,0) through (151.6,18.36,22.35)mm
MATE fastened A.f27 <-> C.f29  axis (0,0,1) through (161,18.36,67.94)mm
